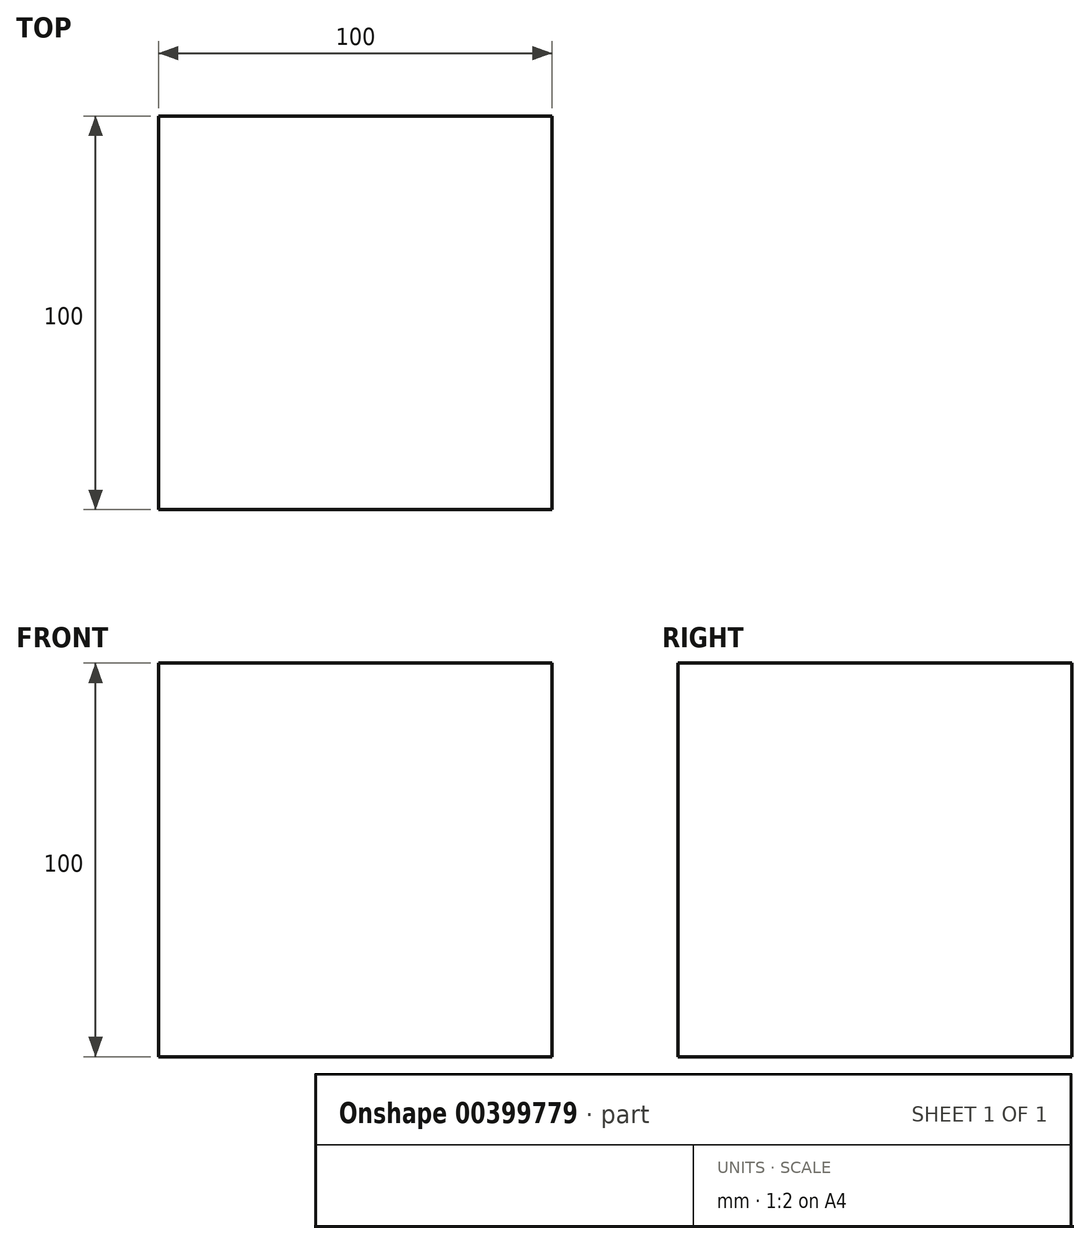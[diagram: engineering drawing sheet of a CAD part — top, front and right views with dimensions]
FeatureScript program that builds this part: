
annotation { "Feature Type Name" : "Feature", "Feature Type Description" : "" }
export const myFeature = defineFeature(function(context is Context, id is Id, definition is map)
    precondition{}
    {
        {
            var Q0;
            Q0=qCreatedBy(makeId("Front.planeOp"),FACE);
            var sketch = newSketch(context, id + "F0", { "sketchPlane" : qUnion([Q0])});
            skLineSegment(sketch, "E0.bottom", {"start": v(-49.52, 37.75) * mm, "end": v(50.48, 37.75) * mm});
            skLineSegment(sketch, "E0.top", {"start": v(-49.52, -62.25) * mm, "end": v(50.48, -62.25) * mm});
            skLineSegment(sketch, "E0.left", {"start": v(-49.52, 37.75) * mm, "end": v(-49.52, -62.25) * mm});
            skLineSegment(sketch, "E0.right", {"start": v(50.48, 37.75) * mm, "end": v(50.48, -62.25) * mm});
            skSolve(sketch);
        }
        {
            var Q0;
            Q0=makeQuery(id+"F0.imprint","IMPRINT",FACE,{"disambiguationData":[TD([[makeQuery(id+"F0.imprint","IMPRINT",EDGE,{"derivedFrom":sQuery(id+"F0.wireOp",EDGE,"E0.bottom")}),-1.0]])]});
            extrude(context, id + "F1", {"entities" : qUnion([Q0]), "depth" : 100 * mm});
        }
    });
